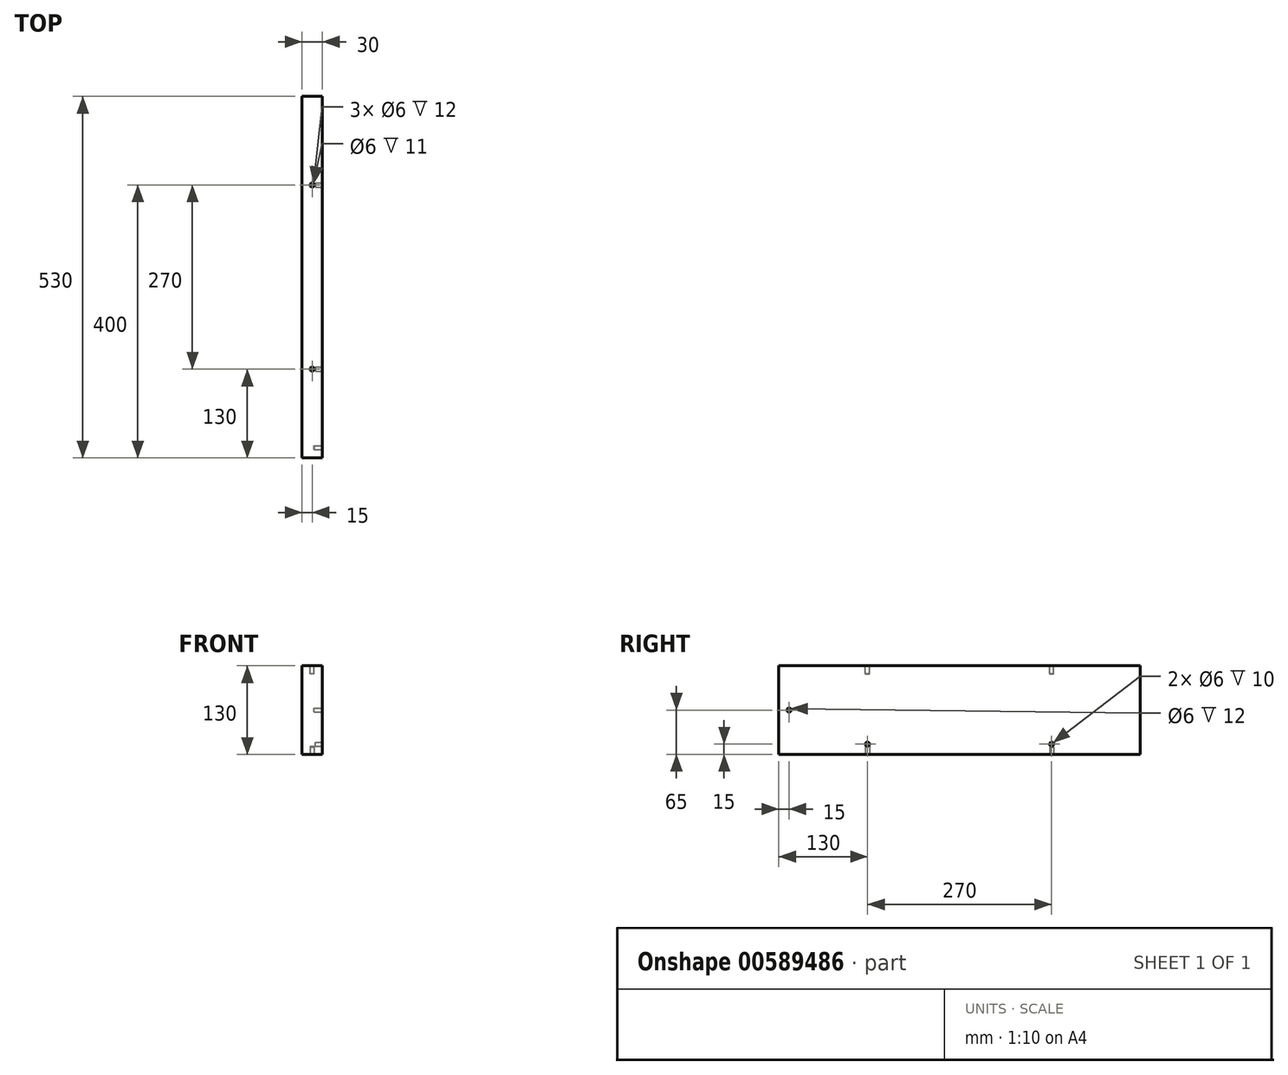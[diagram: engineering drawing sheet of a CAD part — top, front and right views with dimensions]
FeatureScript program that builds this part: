
annotation { "Feature Type Name" : "Feature", "Feature Type Description" : "" }
export const myFeature = defineFeature(function(context is Context, id is Id, definition is map)
    precondition{}
    {
        {
            var Q0;
            Q0=qCreatedBy(makeId("Right.planeOp"),FACE);
            var sketch = newSketch(context, id + "F0", { "sketchPlane" : qUnion([Q0])});
            skLineSegment(sketch, "E0.bottom", {"start": v(0, 0) * mm, "end": v(530, 0) * mm});
            skLineSegment(sketch, "E0.top", {"start": v(0, 130) * mm, "end": v(530, 130) * mm});
            skLineSegment(sketch, "E0.left", {"start": v(0, 0) * mm, "end": v(0, 130) * mm});
            skLineSegment(sketch, "E0.right", {"start": v(530, 0) * mm, "end": v(530, 130) * mm});
            skSolve(sketch);
        }
        {
            var Q0;
            Q0=makeQuery(id+"F0.imprint","IMPRINT",FACE,{"disambiguationData":[TD([[makeQuery(id+"F0.imprint","IMPRINT",EDGE,{"derivedFrom":sQuery(id+"F0.wireOp",EDGE,"E0.bottom")}),1.0]])]});
            extrude(context, id + "F1", {"entities" : qUnion([Q0]), "depth" : 30 * mm, "offsetDistance" : 25 * mm});
        }
        {
            var Q0;
            Q0=makeQuery(id+"F1.opExtrude","SWEPT_FACE",FACE,{"disambiguationData":[OSD([sQuery(id+"F0.wireOp",EDGE,"E0.bottom")])]});
            var sketch = newSketch(context, id + "F2", { "sketchPlane" : qUnion([Q0])});
            skCircle(sketch, "E1", {"center": v(15, -130) * mm, "radius": 3 * mm});
            skPoint(sketch, "E1.centerSnap0", {"position": v(15, 0) * mm});
            skSolve(sketch);
        }
        {
            var Q0;
            Q0=makeQuery(id+"F2.imprint","IMPRINT",FACE,{"disambiguationData":[TD([[makeQuery(id+"F2.imprint","IMPRINT",EDGE,{"derivedFrom":sQuery(id+"F2.wireOp",EDGE,"E1")}),1.0]])]});
            extrude(context, id + "F3", {"entities" : qUnion([Q0]), "operationType" : NewBodyOperationType.REMOVE, "oppositeDirection" : true, "depth" : 12 * mm, "offsetDistance" : 25 * mm});
        }
        {
            var Q0;
            Q0=makeQuery(id+"F1.opExtrude","SWEPT_FACE",FACE,{"disambiguationData":[OSD([sQuery(id+"F0.wireOp",EDGE,"E0.bottom")])]});
            var sketch = newSketch(context, id + "F4", { "sketchPlane" : qUnion([Q0])});
            skCircle(sketch, "E2", {"center": v(15, -400) * mm, "radius": 3 * mm});
            skPoint(sketch, "E2.centerSnap0", {"position": v(15, -530) * mm});
            skSolve(sketch);
        }
        {
            var Q0;
            Q0=makeQuery(id+"F4.imprint","IMPRINT",FACE,{"disambiguationData":[TD([[makeQuery(id+"F4.imprint","IMPRINT",EDGE,{"derivedFrom":sQuery(id+"F4.wireOp",EDGE,"E2")}),1.0]])]});
            extrude(context, id + "F5", {"entities" : qUnion([Q0]), "operationType" : NewBodyOperationType.REMOVE, "oppositeDirection" : true, "depth" : 11 * mm, "offsetDistance" : 25 * mm});
        }
        {
            var Q0;
            Q0=makeQuery(id+"F1.opExtrude","SWEPT_FACE",FACE,{"disambiguationData":[OSD([sQuery(id+"F0.wireOp",EDGE,"E0.top")])]});
            var sketch = newSketch(context, id + "F6", { "sketchPlane" : qUnion([Q0])});
            skCircle(sketch, "E3.0", {"center": v(15, 400) * mm, "radius": 3 * mm});
            skCircle(sketch, "E4.0", {"center": v(15, 130) * mm, "radius": 3 * mm});
            skSolve(sketch);
        }
        {
            var Q0;
            Q0=makeQuery(id+"F6.imprint","IMPRINT",FACE,{"disambiguationData":[TD([[makeQuery(id+"F6.imprint","IMPRINT",EDGE,{"derivedFrom":sQuery(id+"F6.wireOp",EDGE,"E4.0")}),1.0]])]});
            var Q1;
            Q1=makeQuery(id+"F6.imprint","IMPRINT",FACE,{"disambiguationData":[TD([[makeQuery(id+"F6.imprint","IMPRINT",EDGE,{"derivedFrom":sQuery(id+"F6.wireOp",EDGE,"E3.0")}),1.0]])]});
            extrude(context, id + "F7", {"entities" : qUnion([Q0, Q1]), "operationType" : NewBodyOperationType.REMOVE, "oppositeDirection" : true, "depth" : 12 * mm, "offsetDistance" : 25 * mm});
        }
        {
            var Q0;
            Q0=makeQuery(id+"F1.opExtrude","CAP_FACE",FACE,{"disambiguationData":[OSD([sQuery(id+"F0.wireOp",EDGE,"E0.bottom"),sQuery(id+"F0.wireOp",EDGE,"E0.top"),sQuery(id+"F0.wireOp",EDGE,"E0.left"),sQuery(id+"F0.wireOp",EDGE,"E0.right")])],"isStart":false});
            var sketch = newSketch(context, id + "F8", { "sketchPlane" : qUnion([Q0])});
            skCircle(sketch, "E5", {"center": v(130, 15) * mm, "radius": 3 * mm});
            skCircle(sketch, "E6", {"center": v(400, 15) * mm, "radius": 3 * mm});
            skSolve(sketch);
        }
        {
            var Q0;
            Q0=makeQuery(id+"F8.imprint","IMPRINT",FACE,{"disambiguationData":[TD([[makeQuery(id+"F8.imprint","IMPRINT",EDGE,{"derivedFrom":sQuery(id+"F8.wireOp",EDGE,"E6")}),1.0]])]});
            var Q1;
            Q1=makeQuery(id+"F8.imprint","IMPRINT",FACE,{"disambiguationData":[TD([[makeQuery(id+"F8.imprint","IMPRINT",EDGE,{"derivedFrom":sQuery(id+"F8.wireOp",EDGE,"E5")}),1.0]])]});
            extrude(context, id + "F9", {"entities" : qUnion([Q0, Q1]), "operationType" : NewBodyOperationType.REMOVE, "oppositeDirection" : true, "depth" : 10 * mm, "offsetDistance" : 25 * mm});
        }
        {
            var Q0;
            Q0=makeQuery(id+"F1.opExtrude","CAP_FACE",FACE,{"disambiguationData":[OSD([sQuery(id+"F0.wireOp",EDGE,"E0.bottom"),sQuery(id+"F0.wireOp",EDGE,"E0.top"),sQuery(id+"F0.wireOp",EDGE,"E0.left"),sQuery(id+"F0.wireOp",EDGE,"E0.right")])],"isStart":false});
            var sketch = newSketch(context, id + "F10", { "sketchPlane" : qUnion([Q0])});
            skCircle(sketch, "E7", {"center": v(15, 65) * mm, "radius": 3 * mm});
            skSolve(sketch);
        }
        {
            var Q0;
            Q0=makeQuery(id+"F10.imprint","IMPRINT",FACE,{"disambiguationData":[TD([[makeQuery(id+"F10.imprint","IMPRINT",EDGE,{"derivedFrom":sQuery(id+"F10.wireOp",EDGE,"E7")}),1.0]])]});
            extrude(context, id + "F11", {"entities" : qUnion([Q0]), "operationType" : NewBodyOperationType.REMOVE, "oppositeDirection" : true, "depth" : 12 * mm, "offsetDistance" : 25 * mm});
        }
    });
